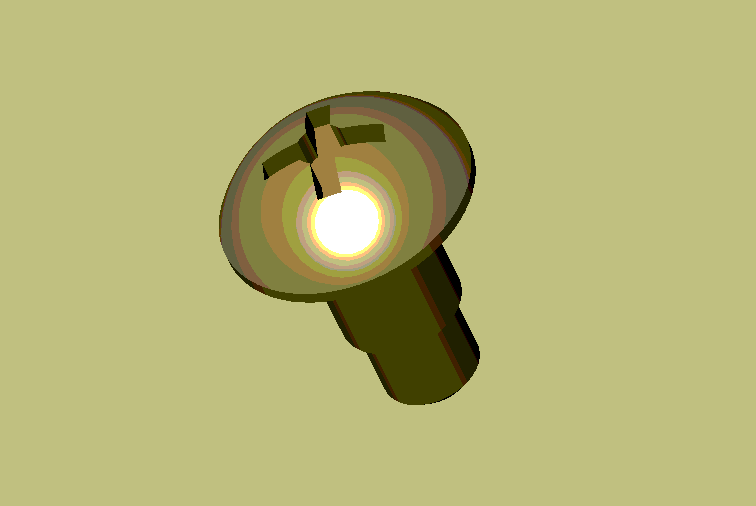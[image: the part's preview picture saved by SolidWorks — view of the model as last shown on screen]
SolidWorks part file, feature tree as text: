
SOLIDWORKS PART (.sldprt)
format: sldprt  version: not decoded by parser v0  size: 190,976 bytes
history: native  units: mm
features: sketch x5, plane x4, extrude x3, material x1, revolve x1, chamfer x1, cut_extrude x1 (+8 scaffold rows collapsed)
feature tree (24):
  scaffold x8  (default folders/planes/origin — collapsed)
  material  "Matériau <non spécifié>"
  plane  "Plane1"
  plane  "Plane2"
  plane  "Plane3"
  sketch  "Esquisse1"  dims[c1.D1=~20.59126mm c1.D2=~20.59126mm c2.D1=12.0mm c2.D2=3.0mm]
  revolve  "Base-Révolution"  Angle=360deg
  sketch  "Esquisse2"
  extrude  "Boss.-Extru.1"  Depth=0.5mm
  sketch  "Esquisse3"  dims[D1=5.0mm]
  extrude  "Boss.-Extru.2"  Depth=6mm
  sketch  "Esquisse4"  dims[D1=4.0mm]
  extrude  "Boss.-Extru.3"  Depth=4mm
  chamfer  "Chanfrein1"  Distance=0.5mm Angle=45deg
  plane  "Plan1"  Offset=4mm
  sketch  "Esquisse5"  dims[D1=2.0mm D2=1.0mm D3=2.5mm]
  cut_extrude  "Enlèv. mat.-Extru.2"  Depth=2mm
decode coverage: 10 of 11 modeling features carry decoded parameters
note: ~ marks probable driven/reference dimensions
note: suppression state not decoded; provenance and decode notes live in map.json
